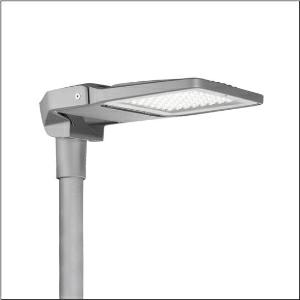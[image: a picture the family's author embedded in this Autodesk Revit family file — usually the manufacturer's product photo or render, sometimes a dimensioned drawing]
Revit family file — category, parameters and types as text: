
# Revit family: floodlight_fl_20_mini___pl61_5xa7672b1c4ac_a92b
name_source: partatom
category: Lighting Fixtures
units: mm (PartAtom-declared; Revit-internal decimal feet)

## family parameters
Cut with Voids When Loaded = No
Host = Face
Light Source = No
Part Type = Normal
Room Calculation Point = No
Round Connector Dimension = Use Diameter
Shared = No

## types (1)
- --- (1 x LED 3000K / CRI = 80 (unbekannt), 4980 lm, 3000K)
    Apparent Load = 51 VA
    CIE Flux Codes = 33 65 98 100 100
    Color Rendering = 80
    Color Temperature = 3000K
    Default Elevation = 1800 mm
    Description = Floodlight FL 20 mini, floodlight, primary light control with lens, of plastic, primary optical cover: protective disc, of toughened safety glass, transparent, light distribution: PL61, light emission: direct distribution, primary light characteristic: asymmetric, installation type: side-entry, post-top, LED, High Power LED, rated luminous flux: 4.980lm, luminous efficacy: 98lm/W, light colour: 830, colour temperature: 3000K, control gear: ECG Plus, control: flexible luminous flux parameterisation, time-dependent luminous flux control, digital communication interface, overheat protection, power reduction, electronic power reduction, with terminal, 5-pole, max. 2.5mm², mains connection: 220..240V, AC, 50/60Hz, rated input power: 51W, LED unit, of diecast aluminium, powder-coated, Siteco® metallic grey (DB 702S), corrosivity category C5 mid according to DIN EN ISO 12944, incl. 1x M20 cable gland for cable Ø 6.5..12mm, inclination adjustable: 0°, 5°, 10°, 15°, please order mast flange separately, length: 565mm, width: 335mm, height: 119mm, housing frame, of diecast aluminium, powder-coated, Siteco® metallic grey (DB 702S), mast flange adapter, of diecast aluminium, powder-coated, Siteco® metallic grey (DB 702S), DALI, protection rating (complete): IP66, insulation class (complete): insulation class II (safety insulation), certification: CE, ENEC, VDE, protection symbol: D, permissible operating ambient temperature: -40..+40°C, permissible operating ambient temperature for outdoor applications: -40..+50°C, standard: DIN EN 12944, packaging unit: 1 piece

Light Distribution: PL61
    Height = 62 mm  [stored 0.203412 ft]
    Lamp = 1 x LED 3000K / CRI >= 80 (unbekannt)
    Lamp Light Flux = 4980 lm
    Lamp count = 1
    Length = 565 mm
    Luminous efficacy = 98 lm/W
    Manufacturer = Siteco
    ModVariant = No
    Model = 5XA7672B1C4AC
    Number of Poles = 1
    OnlyDefault = Yes
    Power Factor = 1
    Product Name = Floodlight FL 20 mini | PL61
    Product group = floodlight | pylon top
    ProductGroupID = 6101
    Protection Class = Protection class II
    Protection Degree = IP 66
    RLX_Detail_Level = 1
    RLX_Emergency_Light_Flux = 0 lm
    RLX_Emergency_Type = 0
    RLX_Emergency_Type_DB = No
    RlxData = <blob elided: 101829 chars, md5=52a61336>
    Socket = socket
    Standby Power = 0 W
    System Light Flux = 4980 lm
    System Power = 51 W
    Type Comments = factory setting: luminous flux: 100 % | dim-lin: 254 | 520 mA
    Type Image = l_1005946.jpg
    URL = http://relux.com
    VarID = @adj_163269
    Voltage = 0 V
    Weight = 0.00 kg
    Width = 335 mm

note: [stored X ft] marks values corroborated as IEEE doubles in the binary element streams (Revit-internal decimal feet)

## geometry (parser evidence)
native form markers: Blend x4, Sweep x13
no freeform markers — native parametric forms only
